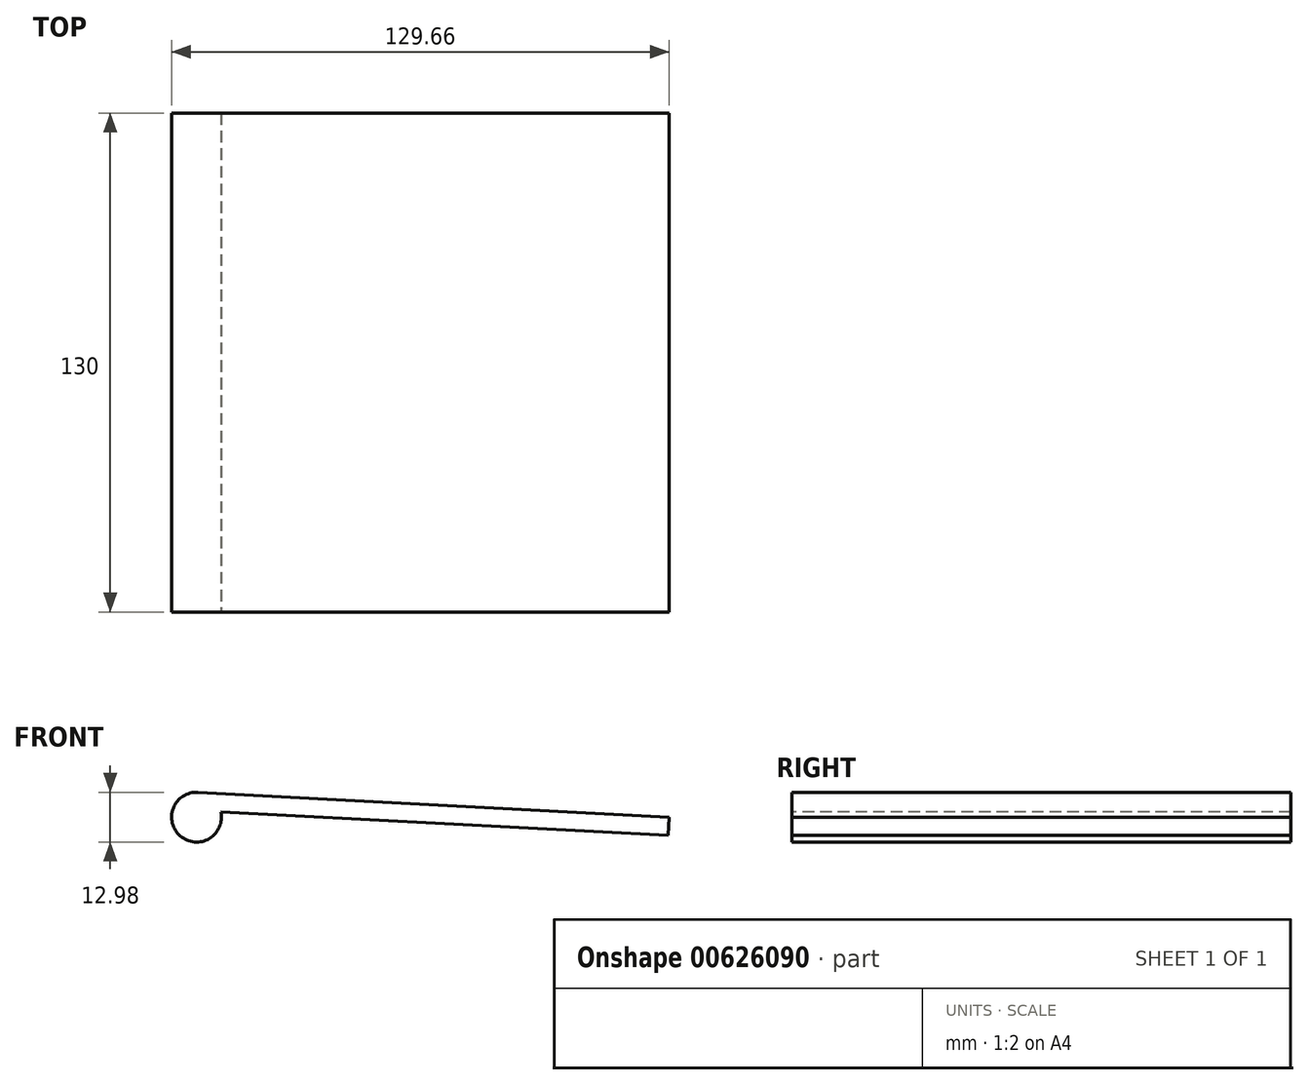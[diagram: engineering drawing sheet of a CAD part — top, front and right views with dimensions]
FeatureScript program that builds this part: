
annotation { "Feature Type Name" : "Feature", "Feature Type Description" : "" }
export const myFeature = defineFeature(function(context is Context, id is Id, definition is map)
    precondition{}
    {
        {
            var Q0;
            Q0=qCreatedBy(makeId("Front.planeOp"),FACE);
            var sketch = newSketch(context, id + "F0", { "sketchPlane" : qUnion([Q0])});
            skArc(sketch, "E0", {"start": v(705.01, 6.49) * mm, "mid": v(700.47, -4.95) * mm, "end": v(711.01, 1.4) * mm});
            skLineSegment(sketch, "E1", {"start": v(705.01, 6.49) * mm, "end": v(827.84, 0) * mm});
            skLineSegment(sketch, "E2", {"start": v(711.01, 1.4) * mm, "end": v(827.59, -4.76) * mm});
            skLineSegment(sketch, "E3", {"start": v(827.59, -4.76) * mm, "end": v(827.84, 0) * mm});
            skSolve(sketch);
        }
        {
            var Q0;
            Q0 = qSketchRegion(id + "F0", true);
            extrude(context, id + "F1", {"entities" : qUnion([Q0]), "oppositeDirection" : true, "depth" : 130 * mm, "offsetDistance" : 25 * mm});
        }
    });
